# Revit family: Drinking_Fountain-Oasis-Bi_Level_Versacooler_II-PG8ACSL
name_source: partatom
category: Plumbing Fixtures
revit_build: Autodesk Revit Architecture 2013 (Build: 20130531_2115(x64)
units: mm (PartAtom-declared; Revit-internal decimal feet)

## types (4) — shared parameters
Apparent Load = 500 VA
Base = Metal - Oasis International - Steel Painted Sandstone - Exterior Finish
Compression HP = 0 VA
Connection Note = Water inlet and outlet location can be adjusted. Contact Oasis for more information.
Default Elevation = 2' - 3"
Description = Barrier-Free Universal Split Level Versacooler II
Manufacturer = Oasis International
Manufacturer Fax Number = (614)322-4557
Number of Poles = 1
Power Factor = 1
Product Documentation Link = http://www.oasiscoolers.com
Product Name = Copper, Bi Level Versacooler II
Product Page URL = http://www.oasiscoolers.com
Rated Watts = 500 W
URL = http://www.oasiscoolers.com
Voltage = 115 V
zero-valued in all types: Cost

## per-type parameters (varying)
| type | Base Rate | Chiller | Full Load Amps | Pre Cooler | Rated Capacity | Top |
| PG8ACSL | 8 GPM | Yes | 4 A | No | 8 GPM | Metal - Oasis International - Steel Painted Sandstone - Exterior Finish |
| PGACSL | 0 GPM | No | 0 A |  | 0 GPM | Metal - Oasis International - Brushed Stainless Steel - Exterior Finish |
| PGACSL CSTN | 0 GPM | No | 0 A |  | 0 GPM | Metal - Oasis International - Brushed Stainless Steel - Exterior Finish |
| PG8ACSL CSTN | 0 GPM | Yes | 0 A |  | 0 GPM | Metal - Oasis International - Brushed Stainless Steel - Exterior Finish |

note: column(s) folded — value = type name in every type: Model

## geometry (parser evidence)
native form markers: Blend x14, Sweep x22
no freeform markers — native parametric forms only
